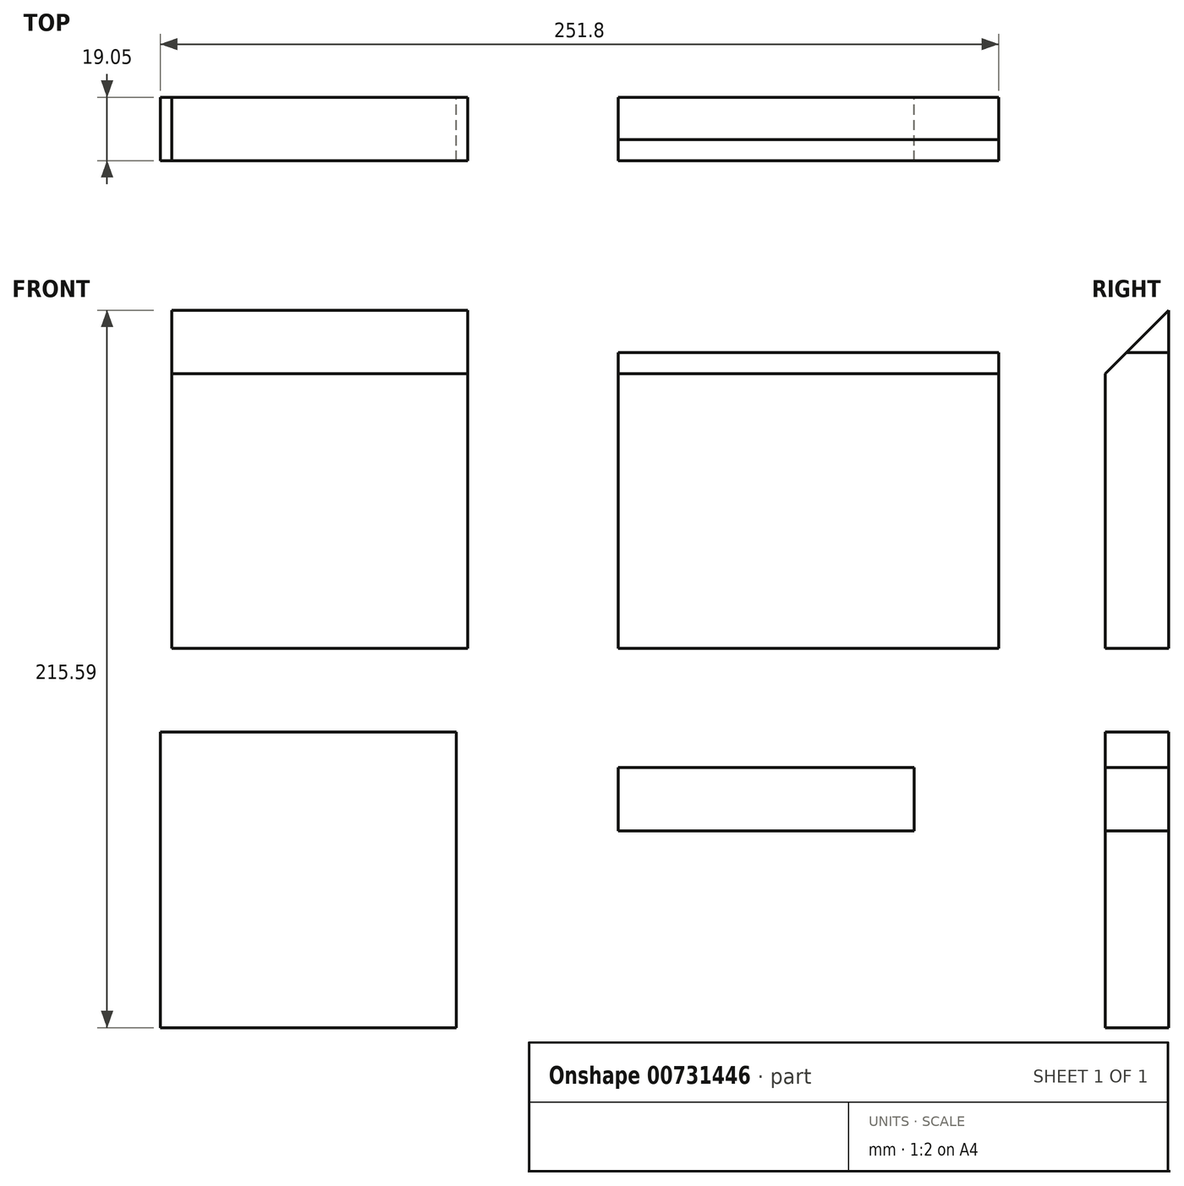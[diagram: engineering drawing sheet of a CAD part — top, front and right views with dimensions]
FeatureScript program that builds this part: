
annotation { "Feature Type Name" : "Feature", "Feature Type Description" : "" }
export const myFeature = defineFeature(function(context is Context, id is Id, definition is map)
    precondition{}
    {
        {
            var Q0;
            Q0=qCreatedBy(makeId("Front.planeOp"),FACE);
            var sketch = newSketch(context, id + "F0", { "sketchPlane" : qUnion([Q0])});
            skLineSegment(sketch, "E0.bottom", {"start": v(0, 0) * mm, "end": v(114.3, 0) * mm});
            skLineSegment(sketch, "E0.top", {"start": v(0, 88.9) * mm, "end": v(114.3, 88.9) * mm});
            skLineSegment(sketch, "E0.left", {"start": v(0, 0) * mm, "end": v(0, 88.9) * mm});
            skLineSegment(sketch, "E0.right", {"start": v(114.3, 0) * mm, "end": v(114.3, 88.9) * mm});
            skSolve(sketch);
        }
        {
            var Q0;
            Q0=qSketchRegion(id+"F0",true);
            extrude(context, id + "F1", {"entities" : qUnion([Q0]), "depth" : 19.05 * mm, "offsetDistance" : 25.4 * mm});
        }
        {
            var Q0;
            Q0=qCreatedBy(makeId("Front.planeOp"),FACE);
            var sketch = newSketch(context, id + "F2", { "sketchPlane" : qUnion([Q0])});
            skLineSegment(sketch, "E1.bottom", {"start": v(0, -35.79) * mm, "end": v(88.9, -35.79) * mm});
            skLineSegment(sketch, "E1.top", {"start": v(0, -54.84) * mm, "end": v(88.9, -54.84) * mm});
            skLineSegment(sketch, "E1.left", {"start": v(0, -35.79) * mm, "end": v(0, -54.84) * mm});
            skLineSegment(sketch, "E1.right", {"start": v(88.9, -35.79) * mm, "end": v(88.9, -54.84) * mm});
            skSolve(sketch);
        }
        {
            var Q0;
            Q0=qSketchRegion(id+"F2",true);
            extrude(context, id + "F3", {"entities" : qUnion([Q0]), "depth" : 19.05 * mm, "offsetDistance" : 25.4 * mm});
        }
        {
            var Q0;
            Q0=qCreatedBy(makeId("Front.planeOp"),FACE);
            var sketch = newSketch(context, id + "F4", { "sketchPlane" : qUnion([Q0])});
            skLineSegment(sketch, "E2.bottom", {"start": v(-45.16, 0) * mm, "end": v(-134.06, 0) * mm});
            skLineSegment(sketch, "E2.top", {"start": v(-45.16, 101.6) * mm, "end": v(-134.06, 101.6) * mm});
            skLineSegment(sketch, "E2.left", {"start": v(-45.16, 0) * mm, "end": v(-45.16, 101.6) * mm});
            skLineSegment(sketch, "E2.right", {"start": v(-134.06, 0) * mm, "end": v(-134.06, 101.6) * mm});
            skSolve(sketch);
        }
        {
            var Q0;
            Q0=qSketchRegion(id+"F4",true);
            extrude(context, id + "F5", {"entities" : qUnion([Q0]), "depth" : 19.05 * mm, "offsetDistance" : 25.4 * mm});
        }
        {
            var Q0;
            Q0=makeQuery(id+"F5.opExtrude","SWEPT_FACE",FACE,{"disambiguationData":[OSD([sQuery(id+"F4.wireOp",EDGE,"E2.right")])]});
            var sketch = newSketch(context, id + "F6", { "sketchPlane" : qUnion([Q0])});
            skLineSegment(sketch, "E3", {"start": v(0, 101.6) * mm, "end": v(19.05, 82.55) * mm});
            skLineSegment(sketch, "E4", {"start": v(19.05, 82.55) * mm, "end": v(19.05, 101.6) * mm});
            skLineSegment(sketch, "E5", {"start": v(19.05, 101.6) * mm, "end": v(0, 101.6) * mm});
            skSolve(sketch);
        }
        {
            var Q0;
            Q0=qSketchRegion(id+"F6",true);
            extrude(context, id + "F7", {"entities" : qUnion([Q0]), "operationType" : NewBodyOperationType.REMOVE, "endBound" : BoundingType.THROUGH_ALL, "oppositeDirection" : true, "depth" : 25.4 * mm, "offsetDistance" : 25.4 * mm});
        }
        {
            var Q0;
            Q0=qCreatedBy(makeId("Front.planeOp"),FACE);
            var sketch = newSketch(context, id + "F8", { "sketchPlane" : qUnion([Q0])});
            skLineSegment(sketch, "E6.bottom", {"start": v(-137.5, -25.1) * mm, "end": v(-48.6, -25.1) * mm});
            skLineSegment(sketch, "E6.top", {"start": v(-137.5, -114) * mm, "end": v(-48.6, -114) * mm});
            skLineSegment(sketch, "E6.left", {"start": v(-137.5, -25.1) * mm, "end": v(-137.5, -114) * mm});
            skLineSegment(sketch, "E6.right", {"start": v(-48.6, -25.1) * mm, "end": v(-48.6, -114) * mm});
            skSolve(sketch);
        }
        {
            var Q0;
            Q0=qSketchRegion(id+"F8",true);
            extrude(context, id + "F9", {"entities" : qUnion([Q0]), "depth" : 19.05 * mm, "offsetDistance" : 25.4 * mm});
        }
    });
